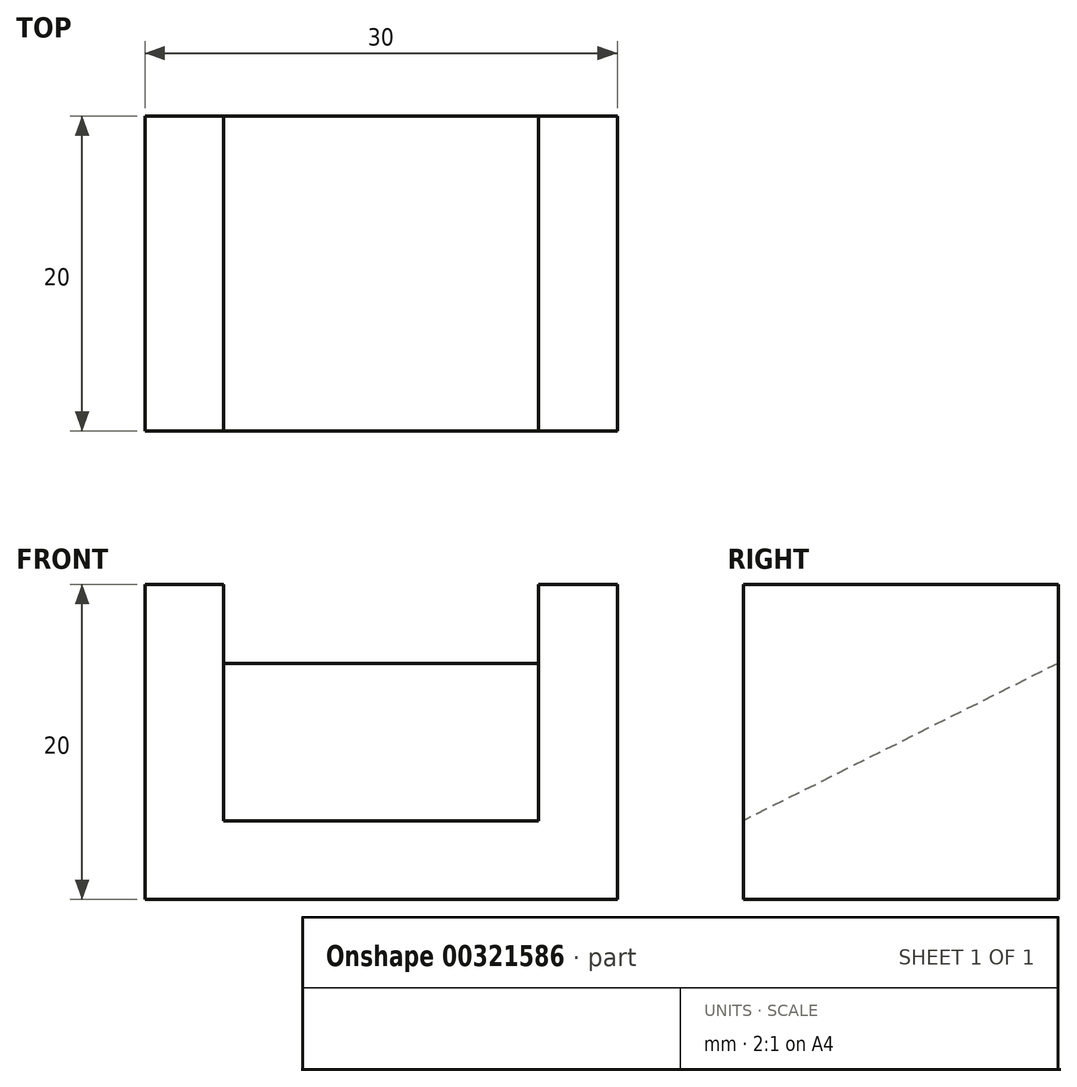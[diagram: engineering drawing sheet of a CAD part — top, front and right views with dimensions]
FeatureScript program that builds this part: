
annotation { "Feature Type Name" : "Feature", "Feature Type Description" : "" }
export const myFeature = defineFeature(function(context is Context, id is Id, definition is map)
    precondition{}
    {
        {
            var Q0;
            Q0=qCreatedBy(makeId("Right.planeOp"),FACE);
            var sketch = newSketch(context, id + "F0", { "sketchPlane" : qUnion([Q0])});
            skLineSegment(sketch, "E0", {"start": v(0, 0) * mm, "end": v(20, 0) * mm});
            skLineSegment(sketch, "E1", {"start": v(20, 0) * mm, "end": v(20, 20) * mm});
            skLineSegment(sketch, "E2", {"start": v(20, 20) * mm, "end": v(0, 20) * mm});
            skLineSegment(sketch, "E3", {"start": v(0, 20) * mm, "end": v(0, 0) * mm});
            skSolve(sketch);
        }
        {
            var Q0;
            Q0 = qSketchRegion(id + "F0", true);
            extrude(context, id + "F1", {"entities" : qUnion([Q0]), "depth" : 30 * mm});
        }
        {
            var Q0;
            Q0=makeQuery(id+"F1.opExtrude","CAP_FACE",FACE,{"disambiguationData":[OSD([sQuery(id+"F0.wireOp",EDGE,"E0"),sQuery(id+"F0.wireOp",EDGE,"E1"),sQuery(id+"F0.wireOp",EDGE,"E2"),sQuery(id+"F0.wireOp",EDGE,"E3")])],"isStart":false});
            var sketch = newSketch(context, id + "F2", { "sketchPlane" : qUnion([Q0])});
            skLineSegment(sketch, "E4", {"start": v(20, 15) * mm, "end": v(0, 5) * mm});
            skLineSegment(sketch, "E5", {"start": v(0, 5) * mm, "end": v(20, 5) * mm});
            skLineSegment(sketch, "E6", {"start": v(20, 5) * mm, "end": v(20, 15) * mm});
            skSolve(sketch);
        }
        {
            var Q0;
            {var subQ0=sQuery(id+"F2.wireOp",EDGE,"E4");Q0=makeQuery(id+"F2.imprint","IMPRINT",FACE,{"disambiguationData":[TD([[makeQuery(id+"F2.imprint","IMPRINT",EDGE,{"derivedFrom":subQ0}),-1.0]])]});}
            extrude(context, id + "F3", {"entities" : qUnion([Q0]), "operationType" : NewBodyOperationType.REMOVE, "oppositeDirection" : true, "depth" : 25 * mm, "hasSecondDirection" : true, "secondDirectionOppositeDirection" : true, "secondDirectionDepth" : 5 * mm});
        }
    });
